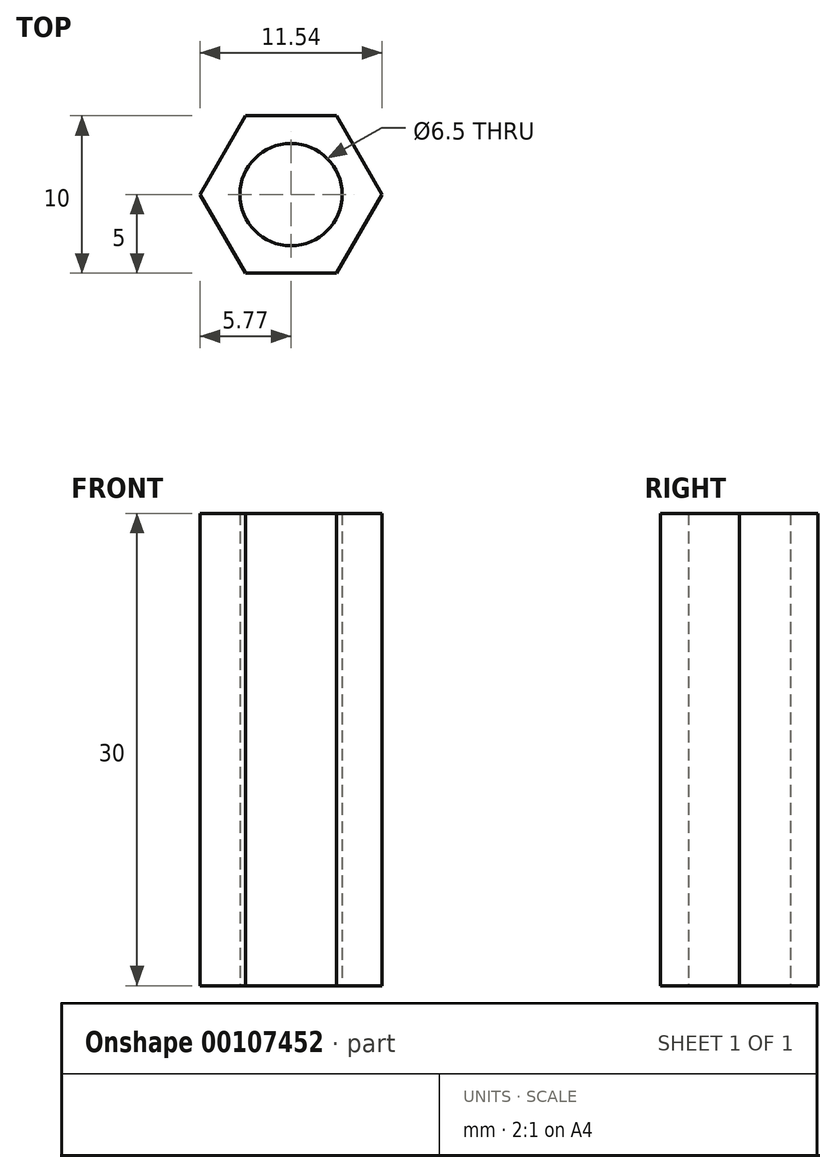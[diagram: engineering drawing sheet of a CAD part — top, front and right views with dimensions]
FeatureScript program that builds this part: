
annotation { "Feature Type Name" : "Feature", "Feature Type Description" : "" }
export const myFeature = defineFeature(function(context is Context, id is Id, definition is map)
    precondition{}
    {
        {
            var Q0;
            Q0=qCreatedBy(makeId("Top.planeOp"),FACE);
            var sketch = newSketch(context, id + "F0", { "sketchPlane" : qUnion([Q0])});
            skCircle(sketch, "E0.cCircle", {"center": v(0, 0) * mm, "radius": 5 * mm, "construction": true});
            skLineSegment(sketch, "E0.0", {"start": v(2.89, -5) * mm, "end": v(-2.89, -5) * mm});
            skLineSegment(sketch, "E0.1", {"start": v(-2.89, -5) * mm, "end": v(-5.77, 0) * mm});
            skLineSegment(sketch, "E0.2", {"start": v(-5.77, 0) * mm, "end": v(-2.89, 5) * mm});
            skLineSegment(sketch, "E0.3", {"start": v(-2.89, 5) * mm, "end": v(2.89, 5) * mm});
            skLineSegment(sketch, "E0.4", {"start": v(2.89, 5) * mm, "end": v(5.77, 0) * mm});
            skLineSegment(sketch, "E0.5", {"start": v(5.77, 0) * mm, "end": v(2.89, -5) * mm});
            skPoint(sketch, "E0.0.midPoint", {"position": v(0, -5) * mm});
            skCircle(sketch, "E1", {"center": v(0, 0) * mm, "radius": 3.25 * mm});
            skSolve(sketch);
        }
        {
            var Q0;
            Q0=makeQuery(id+"F0.imprint","IMPRINT",FACE,{"disambiguationData":[TD([[makeQuery(id+"F0.imprint","IMPRINT",EDGE,{"derivedFrom":sQuery(id+"F0.wireOp",EDGE,"E0.0")}),-1.0]])]});
            extrude(context, id + "F1", {"entities" : qUnion([Q0]), "endBound" : BoundingType.SYMMETRIC, "depth" : 30 * mm});
        }
    });
